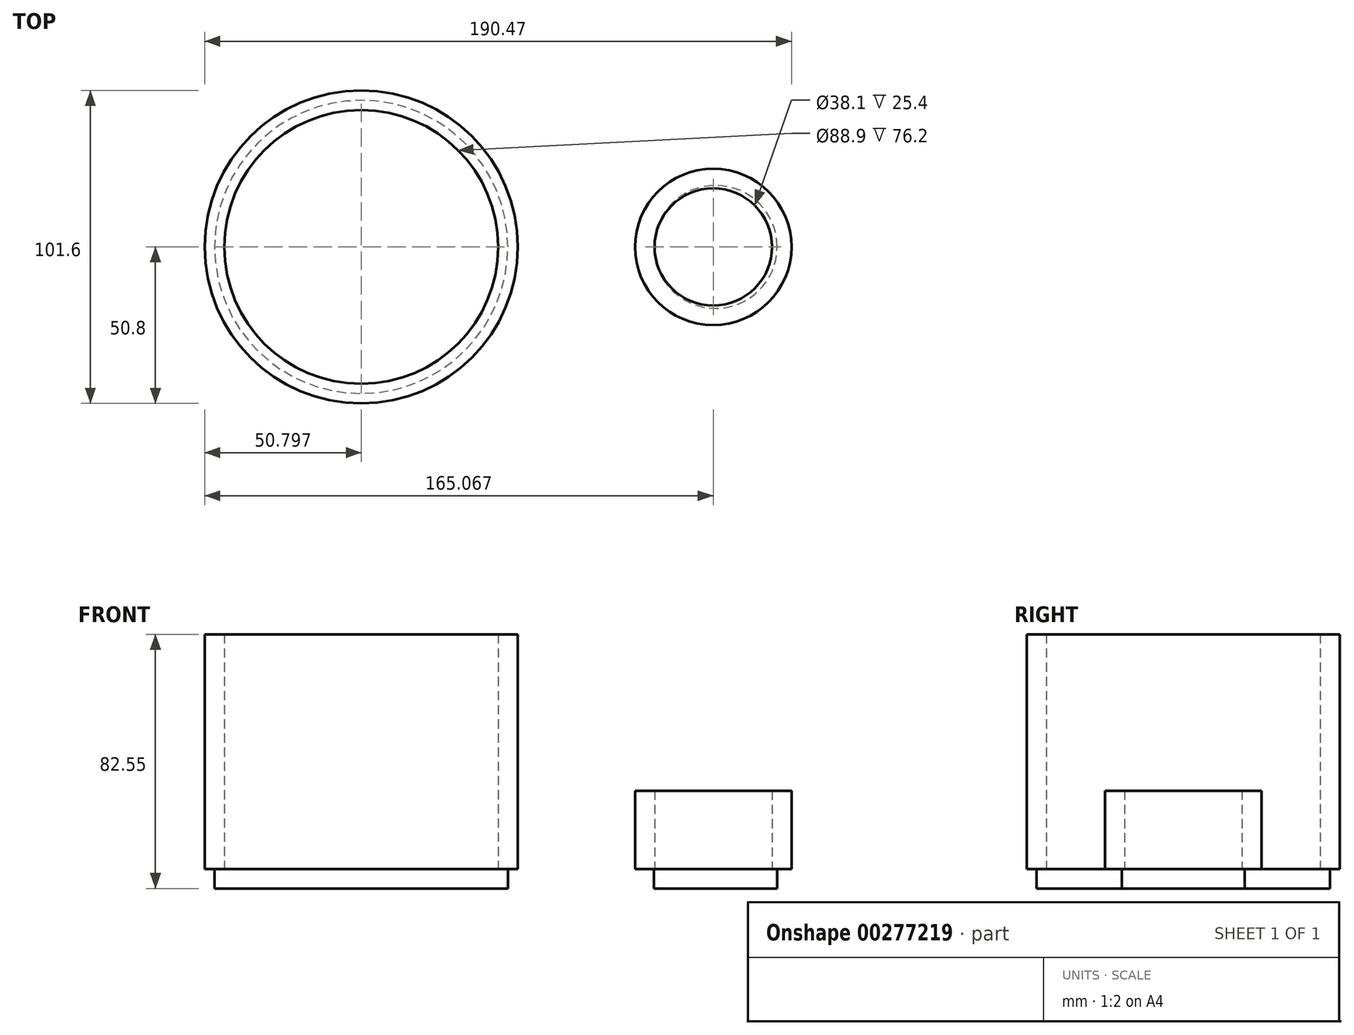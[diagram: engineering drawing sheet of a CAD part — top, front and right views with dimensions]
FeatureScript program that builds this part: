
annotation { "Feature Type Name" : "Feature", "Feature Type Description" : "" }
export const myFeature = defineFeature(function(context is Context, id is Id, definition is map)
    precondition{}
    {
        {
            var Q0;
            Q0=qCreatedBy(makeId("Top.planeOp"),FACE);
            var sketch = newSketch(context, id + "F0", { "sketchPlane" : qUnion([Q0])});
            skCircle(sketch, "E0", {"center": v(-73.26, 0) * mm, "radius": 50.8 * mm});
            skCircle(sketch, "E1", {"center": v(-73.26, 0) * mm, "radius": 44.45 * mm});
            skSolve(sketch);
        }
        {
            var Q0;
            Q0=makeQuery(id+"F0.imprint","IMPRINT",FACE,{"disambiguationData":[TD([[makeQuery(id+"F0.imprint","IMPRINT",EDGE,{"derivedFrom":sQuery(id+"F0.wireOp",EDGE,"E0")}),1.0]])]});
            extrude(context, id + "F1", {"entities" : qUnion([Q0]), "depth" : 76.2 * mm});
        }
        {
            var Q0;
            Q0=makeQuery(id+"F1.opExtrude","CAP_FACE",FACE,{"disambiguationData":[OSD([sQuery(id+"F0.wireOp",EDGE,"E0"),sQuery(id+"F0.wireOp",EDGE,"E1")])],"isStart":true});
            var sketch = newSketch(context, id + "F2", { "sketchPlane" : qUnion([Q0])});
            skCircle(sketch, "E2", {"center": v(-73.26, 0) * mm, "radius": 47.59 * mm});
            skSolve(sketch);
        }
        {
            var Q0;
            Q0 = qSketchRegion(id + "F2", true);
            extrude(context, id + "F3", {"entities" : qUnion([Q0]), "operationType" : NewBodyOperationType.ADD, "depth" : 6.35 * mm});
        }
        {
            var Q0;
            Q0=qCreatedBy(makeId("Top.planeOp"),FACE);
            var sketch = newSketch(context, id + "F4", { "sketchPlane" : qUnion([Q0])});
            skCircle(sketch, "E3", {"center": v(41, 0) * mm, "radius": 25.4 * mm});
            skCircle(sketch, "E4", {"center": v(41, 0) * mm, "radius": 19.05 * mm});
            skSolve(sketch);
        }
        {
            var Q0;
            Q0=makeQuery(id+"F4.imprint","IMPRINT",FACE,{"disambiguationData":[TD([[makeQuery(id+"F4.imprint","IMPRINT",EDGE,{"derivedFrom":sQuery(id+"F4.wireOp",EDGE,"E3")}),1.0]])]});
            extrude(context, id + "F5", {"entities" : qUnion([Q0]), "depth" : 25.4 * mm});
        }
        {
            var Q0;
            Q0=qCreatedBy(makeId("Top.planeOp"),FACE);
            var sketch = newSketch(context, id + "F6", { "sketchPlane" : qUnion([Q0])});
            skCircle(sketch, "E5", {"center": v(41.77, 0) * mm, "radius": 19.97 * mm});
            skSolve(sketch);
        }
        {
            var Q0;
            Q0 = qSketchRegion(id + "F6", true);
            extrude(context, id + "F7", {"entities" : qUnion([Q0]), "operationType" : NewBodyOperationType.ADD, "oppositeDirection" : true, "depth" : 6.35 * mm});
        }
    });
